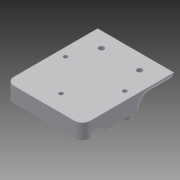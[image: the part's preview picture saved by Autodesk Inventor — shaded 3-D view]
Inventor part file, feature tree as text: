
AUTODESK INVENTOR PART (.ipt)
format: ipt  version: 2014 (Build 180170000, 170)  size: 326,656 bytes
history: native  units: in
note: dims shown in document units (in); Inventor stores cm internally (conversion verified against a paired STEP export)
features: sketch x13, extrude x7, mirror x4, fillet x4, revolve x3, projected_geometry x3, plane x2, other x2, hole x2
ambient origin geometry x8: Origin, YZ Plane, XZ Plane, XY Plane, X Axis, Y Axis, Z Axis, Center Point
bodies: Solid1 (feature_tree)
feature tree (40):
  sketch  "Sketch1"  dims[d0=2.5in d1=2.0in]
  extrude  "Extrusion1"  Depth=2.5in
  plane  "Work Plane1"
  plane  "Work Plane2"
  extrude  "Extrusion2"  TaperAngle=120.0deg  [1 undecoded]
  mirror  "Mirror2"
  extrude  "Extrusion4"  TaperAngle=120.0deg  [1 undecoded]
  sketch  "Sketch6"  dims[d6=0.5in d7=0.0in d9=-0.2061in]
  other  "Work Axis1"
  revolve  "Revolution1"  [1 undecoded]
  mirror  "Mirror3"
  sketch  "Sketch11"  dims[d10=0.38in d11=0.5in d12=0.0in]
  other  "Work Axis2"
  revolve  "Revolution4"  [1 undecoded]
  extrude  "Extrusion5"  Depth=0.28in
  extrude  "Extrusion6"  Depth=0.105in
  mirror  "Mirror4"
  sketch  "Sketch14"  dims[d22=90.0deg d23=0.075in]
  extrude  "Extrusion7"  Depth=0.075in
  hole  "Hole1"  [1 undecoded]
  fillet  "Fillet1"  Radius=2.0in
  revolve  "Revolution5"  [1 undecoded]
  mirror  "Mirror5"
  extrude  "Extrusion8"  Depth=1.25in
  fillet  "Fillet2"  Radius=0.025in
  fillet  "Fillet3"  Radius=0.025in
  fillet  "Fillet4"  Radius=0.05in
  hole  "Hole2"  [1 undecoded]
  sketch  "Sketch2"  dims[d2=0.8in d3=120.0deg]
  sketch  "Sketch5"  dims[d4=150.0deg d5=120.0deg]
  sketch  "Sketch12"  dims[d13=90.0deg d18=0.28in]
  sketch  "Sketch13"  dims[d19=0.8in d20=0.0in d21=0.105in]
  sketch  "Sketch15"  dims[d33=0.08in d34=180.0deg d35=2.0in]
  sketch  "Sketch16"  dims[d36=0.025in d37=0.025in]
  projected_geometry  "Projected Loop1"
  projected_geometry  "Projected Loop2"
  projected_geometry  "Projected Loop3"
  sketch  "Sketch17"  dims[d38=0.05in d39=0.0in d40=1.25in d41=0.025in d42=0.025in d43=0.05in d44=0.0in]
  sketch  "Sketch18"  dims[d45=0.425in d46=0.83in]
  sketch  "Sketch19"  dims[d47=0.4in d48=0.4in d49=0.4in d50=0.245in d51=0.0in d52=0.136in d53=0.75in d54=0.375in d55=0.25in d56=0.5635in d57=1.0in d58=0.8108in d59=0.0625in d60=0.1in d61=0.0625in d62=180.0deg d63=1.0in d64=0.0in d65=0.25in d66=0.25in d67=0.25in d68=0.375in d69=0.375in d71=0.173in d72=0.75in d73=0.375in d74=0.25in d75=0.5635in d76=1.0in d77=0.8108in]
note: 7 required parameter values undecoded (feature->parameter linkage not recoverable at this tier; creation-order binding heuristic only, values carry confidence <= 0.55)